# Revit family: IS_Prosys_R0105_BIM_DE
name_source: partatom
category: Plumbing Fixtures
revit_build: Autodesk Revit 2017 (Build: 20160225_1515(x64)
units: mm (PartAtom-declared; Revit-internal decimal feet)

## family parameters
Cut with Voids When Loaded = No
Host = Face
OmniClass Number = 23.45.05.21.11.11
OmniClass Title = Water Operated Water Closets
Part Type = Normal
Room Calculation Point = No
Round Connector Dimension = Use Diameter
Shared = Yes

## types (1)
- R010567 - PROSYS FRAME FOR ACCESSORIES/GRBRLS
    Accessories = https://www.idealstandardnederland.nl
    AreaUnits = millimeters
    Assembly Code = C1030200
    AssetType = Fixed
    BIMObjectName = IS_IdealStandard_UrinalandWCfittings_Prosys_R0105
    BREEAMApproved = No
    BarCode = 3391500579644
    Brand = Ideal Standard Netherlands
    CWFU = 0
    ConnectionType = Plumbing
    Cost = 0 $
    CurrencyUnit = €
    Default Elevation = 0 mm  [stored 0 ft]
    Description = PROSYS FRAME FOR ACCESSORIES / GRBRLS
    DurationUnit = year
    ECA = No
    ExpectedLife = 30
    Features = FRAME FOR ACCESSORIES/GRBRLS
    Finish = White
    HWFU = 0
    Help = https://www.idealstandardnederland.nl
    IfcExportAs = IfcSanitaryTerminalType
    IfcExportType = CISTERN
    InstallationInstructions = https://www.idealstandardnederland.nl
    LinearUnits = millimeters
    Manufacturer = https://www.idealstandardnederland.nl
    ManufacturerURL = https://www.idealstandardnederland.nl
    Model = R0105
    ModelNumber = R0105
    ModelReference = PROSYS FRAME FOR ACCESSORIES / GRBRLS
    NBSDescription = WC cistern fittings
    NBSReference = 45-30-70/387
    Name = UrinalandWCfittings_Prosys_R0105_IdealStandard
    NettWeight = 4.32 Kg
    NominalDepth = 115 mm  [stored 0.377297 ft]
    NominalHeight = 1150 mm
    NominalLength = 115 mm  [stored 0.377297 ft]
    NominalWidth = 240 mm  [stored 0.787402 ft]
    ProductInformation = https://www.idealstandardnederland.nl
    Shape = Sculptured
    Size = 340 x 226 x 1145 mm
    Space = Internal
    SpilloverLevel = 0 mm  [stored 0 ft]
    ToiletPanType = WashDown
    ToiletType = Other
    URL = https://www.idealstandardnederland.nl
    Uniclass2 = Pr_40_20_93_89
    Uniclass2015Code = Pr_40_20_93
    Uniclass2015Description = Urinal and WC fittings
    Uniclass2015Reference = Pr_40_20_93
    Uniclass2015Title = Urinal and WC fittings
    Uniclass2015Version = v1.1
    Version = 1
    VolumeUnits = Litres
    WFU = 0
    WRAS = No
    WarrantyDescription = Manufacturers Warranty
    WarrantyDurationParts = 0
    WarrantyDurationUnit = year
    WarrantyGuarantorParts = https://www.idealstandardnederland.nl
    WaterEfficientProduct = No

note: [stored X ft] marks values corroborated as IEEE doubles in the binary element streams (Revit-internal decimal feet)

## geometry (parser evidence)
native form markers: Sweep x1
no freeform markers — native parametric forms only
